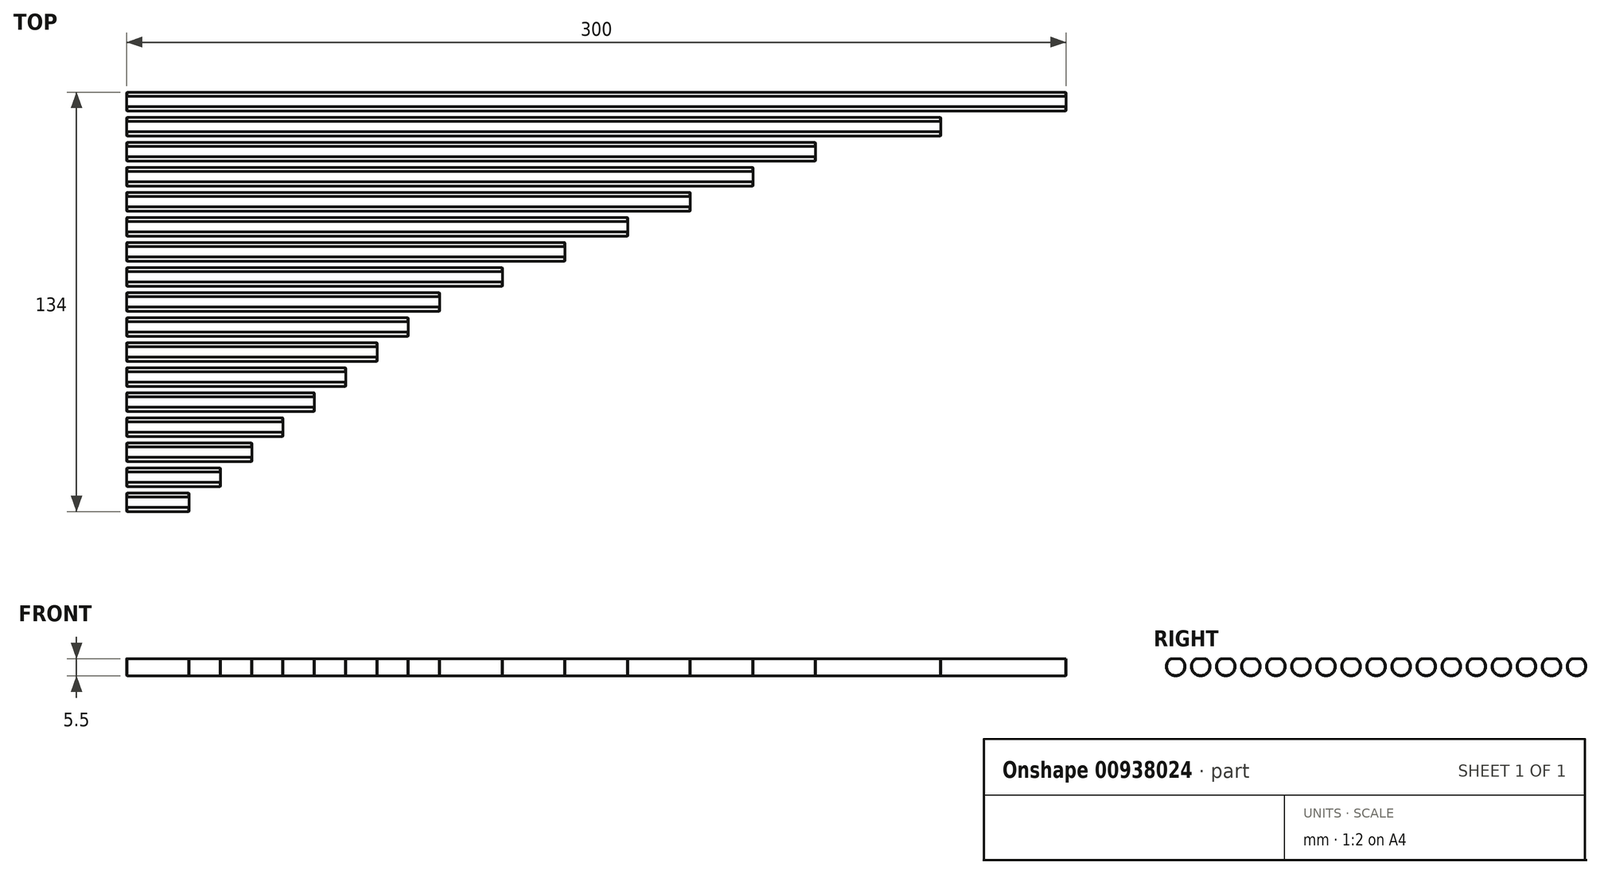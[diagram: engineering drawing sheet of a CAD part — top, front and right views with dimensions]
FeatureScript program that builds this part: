
annotation { "Feature Type Name" : "Feature", "Feature Type Description" : "" }
export const myFeature = defineFeature(function(context is Context, id is Id, definition is map)
    precondition{}
    {
        {
            var Q0;
            Q0=qCreatedBy(makeId("Right.planeOp"),FACE);
            var sketch = newSketch(context, id + "F0", { "sketchPlane" : qUnion([Q0]) });
            skLineSegment(sketch, "E0", {"start": v(0, 3) * mm, "end": v(128, 3) * mm, "construction": true});
            skCircle(sketch, "E1", {"center": v(0, 0) * mm, "radius": 3 * mm});
            skCircle(sketch, "E2", {"center": v(8, 0) * mm, "radius": 3 * mm});
            skCircle(sketch, "E3", {"center": v(16, 0) * mm, "radius": 3 * mm});
            skCircle(sketch, "E4", {"center": v(24, 0) * mm, "radius": 3 * mm});
            skCircle(sketch, "E5", {"center": v(32, 0) * mm, "radius": 3 * mm});
            skCircle(sketch, "E6", {"center": v(40, 0) * mm, "radius": 3 * mm});
            skCircle(sketch, "E7", {"center": v(48, 0) * mm, "radius": 3 * mm});
            skCircle(sketch, "E8", {"center": v(56, 0) * mm, "radius": 3 * mm});
            skCircle(sketch, "E9", {"center": v(64, 0) * mm, "radius": 3 * mm});
            skCircle(sketch, "E10", {"center": v(72, 0) * mm, "radius": 3 * mm});
            skCircle(sketch, "E11", {"center": v(80, 0) * mm, "radius": 3 * mm});
            skLineSegment(sketch, "E12", {"start": v(0, 0) * mm, "end": v(8, 0) * mm, "construction": true});
            skLineSegment(sketch, "E13", {"start": v(16, 0) * mm, "end": v(24, 0) * mm, "construction": true});
            skLineSegment(sketch, "E14", {"start": v(32, 0) * mm, "end": v(40, 0) * mm, "construction": true});
            skLineSegment(sketch, "E15", {"start": v(48, 0) * mm, "end": v(40, 0) * mm, "construction": true});
            skLineSegment(sketch, "E16", {"start": v(24, 0) * mm, "end": v(32, 0) * mm, "construction": true});
            skLineSegment(sketch, "E17", {"start": v(8, 0) * mm, "end": v(16, 0) * mm, "construction": true});
            skLineSegment(sketch, "E18", {"start": v(48, 0) * mm, "end": v(56, 0) * mm, "construction": true});
            skLineSegment(sketch, "E19", {"start": v(56, 0) * mm, "end": v(64, 0) * mm, "construction": true});
            skLineSegment(sketch, "E20", {"start": v(64, 0) * mm, "end": v(72, 0) * mm, "construction": true});
            skLineSegment(sketch, "E21", {"start": v(72, 0) * mm, "end": v(80, 0) * mm, "construction": true});
            skLineSegment(sketch, "E22", {"start": v(80, 0) * mm, "end": v(88, 0) * mm, "construction": true});
            skLineSegment(sketch, "E23", {"start": v(88, 0) * mm, "end": v(96, 0) * mm, "construction": true});
            skLineSegment(sketch, "E24", {"start": v(96, 0) * mm, "end": v(104, 0) * mm, "construction": true});
            skLineSegment(sketch, "E25", {"start": v(104, 0) * mm, "end": v(112, 0) * mm, "construction": true});
            skLineSegment(sketch, "E26", {"start": v(112, 0) * mm, "end": v(120, 0) * mm, "construction": true});
            skCircle(sketch, "E27", {"center": v(88, 0) * mm, "radius": 3 * mm});
            skCircle(sketch, "E28", {"center": v(96, 0) * mm, "radius": 3 * mm});
            skCircle(sketch, "E29", {"center": v(104, 0) * mm, "radius": 3 * mm});
            skCircle(sketch, "E30", {"center": v(112, 0) * mm, "radius": 3 * mm});
            skCircle(sketch, "E31", {"center": v(120, 0) * mm, "radius": 3 * mm});
            skLineSegment(sketch, "E32", {"start": v(120, 0) * mm, "end": v(128, 0) * mm, "construction": true});
            skCircle(sketch, "E33", {"center": v(128, 0) * mm, "radius": 3 * mm});
            skLineSegment(sketch, "E34", {"start": v(-1.66, 2.5) * mm, "end": v(1.66, 2.5) * mm});
            skLineSegment(sketch, "E35.trimOffspring", {"start": v(6.34, 2.5) * mm, "end": v(9.66, 2.5) * mm});
            skLineSegment(sketch, "E36.trimOffspring", {"start": v(14.34, 2.5) * mm, "end": v(17.66, 2.5) * mm});
            skLineSegment(sketch, "E37.trimOffspring", {"start": v(22.34, 2.5) * mm, "end": v(25.66, 2.5) * mm});
            skLineSegment(sketch, "E38.trimOffspring", {"start": v(30.34, 2.5) * mm, "end": v(33.66, 2.5) * mm});
            skLineSegment(sketch, "E39.trimOffspring", {"start": v(38.34, 2.5) * mm, "end": v(41.66, 2.5) * mm});
            skLineSegment(sketch, "E40.trimOffspring", {"start": v(46.34, 2.5) * mm, "end": v(49.66, 2.5) * mm});
            skLineSegment(sketch, "E41.trimOffspring", {"start": v(54.34, 2.5) * mm, "end": v(57.66, 2.5) * mm});
            skLineSegment(sketch, "E42.trimOffspring", {"start": v(62.34, 2.5) * mm, "end": v(65.66, 2.5) * mm});
            skLineSegment(sketch, "E43.trimOffspring", {"start": v(78.34, 2.5) * mm, "end": v(81.66, 2.5) * mm});
            skLineSegment(sketch, "E44.trimOffspring", {"start": v(70.34, 2.5) * mm, "end": v(73.66, 2.5) * mm});
            skLineSegment(sketch, "E45.trimOffspring", {"start": v(86.34, 2.5) * mm, "end": v(89.66, 2.5) * mm});
            skLineSegment(sketch, "E46.trimOffspring", {"start": v(94.34, 2.5) * mm, "end": v(97.66, 2.5) * mm});
            skLineSegment(sketch, "E47.trimOffspring", {"start": v(102.34, 2.5) * mm, "end": v(105.66, 2.5) * mm});
            skLineSegment(sketch, "E48.trimOffspring", {"start": v(110.34, 2.5) * mm, "end": v(113.66, 2.5) * mm});
            skLineSegment(sketch, "E49.trimOffspring", {"start": v(118.34, 2.5) * mm, "end": v(121.66, 2.5) * mm});
            skLineSegment(sketch, "E50.trimOffspring", {"start": v(126.34, 2.5) * mm, "end": v(129.66, 2.5) * mm});
            skSolve(sketch);
        }
        {
            var Q0;
            {var subQ0=sQuery(id+"F0.wireOp",EDGE,"E34");Q0=makeQuery(id+"F0.imprint","IMPRINT",FACE,{"disambiguationData":[TD([[makeQuery(id+"F0.imprint","IMPRINT",EDGE,{"derivedFrom":subQ0}),-1.0]])]});}
            extrude(context, id + "F1", {"entities" : qUnion([Q0]), "depth" : 20 * mm, "offsetDistance" : 25 * mm});
        }
        {
            var Q0;
            {var subQ0=sQuery(id+"F0.wireOp",EDGE,"E35.trimOffspring");Q0=makeQuery(id+"F0.imprint","IMPRINT",FACE,{"disambiguationData":[TD([[makeQuery(id+"F0.imprint","IMPRINT",EDGE,{"derivedFrom":subQ0}),-1.0]])]});}
            extrude(context, id + "F2", {"entities" : qUnion([Q0]), "depth" : 30 * mm, "offsetDistance" : 25 * mm});
        }
        {
            var Q0;
            {var subQ0=sQuery(id+"F0.wireOp",EDGE,"E36.trimOffspring");Q0=makeQuery(id+"F0.imprint","IMPRINT",FACE,{"disambiguationData":[TD([[makeQuery(id+"F0.imprint","IMPRINT",EDGE,{"derivedFrom":subQ0}),-1.0]])]});}
            extrude(context, id + "F3", {"entities" : qUnion([Q0]), "depth" : 40 * mm, "offsetDistance" : 25 * mm});
        }
        {
            var Q0;
            {var subQ0=sQuery(id+"F0.wireOp",EDGE,"E37.trimOffspring");Q0=makeQuery(id+"F0.imprint","IMPRINT",FACE,{"disambiguationData":[TD([[makeQuery(id+"F0.imprint","IMPRINT",EDGE,{"derivedFrom":subQ0}),-1.0]])]});}
            extrude(context, id + "F4", {"entities" : qUnion([Q0]), "depth" : 50 * mm, "offsetDistance" : 25 * mm});
        }
        {
            var Q0;
            {var subQ0=sQuery(id+"F0.wireOp",EDGE,"E38.trimOffspring");Q0=makeQuery(id+"F0.imprint","IMPRINT",FACE,{"disambiguationData":[TD([[makeQuery(id+"F0.imprint","IMPRINT",EDGE,{"derivedFrom":subQ0}),-1.0]])]});}
            extrude(context, id + "F5", {"entities" : qUnion([Q0]), "depth" : 60 * mm, "offsetDistance" : 25 * mm});
        }
        {
            var Q0;
            {var subQ0=sQuery(id+"F0.wireOp",EDGE,"E39.trimOffspring");Q0=makeQuery(id+"F0.imprint","IMPRINT",FACE,{"disambiguationData":[TD([[makeQuery(id+"F0.imprint","IMPRINT",EDGE,{"derivedFrom":subQ0}),-1.0]])]});}
            extrude(context, id + "F6", {"entities" : qUnion([Q0]), "depth" : 70 * mm, "offsetDistance" : 25 * mm});
        }
        {
            var Q0;
            {var subQ0=sQuery(id+"F0.wireOp",EDGE,"E40.trimOffspring");Q0=makeQuery(id+"F0.imprint","IMPRINT",FACE,{"disambiguationData":[TD([[makeQuery(id+"F0.imprint","IMPRINT",EDGE,{"derivedFrom":subQ0}),-1.0]])]});}
            extrude(context, id + "F7", {"entities" : qUnion([Q0]), "depth" : 80 * mm, "offsetDistance" : 25 * mm});
        }
        {
            var Q0;
            {var subQ0=sQuery(id+"F0.wireOp",EDGE,"E41.trimOffspring");Q0=makeQuery(id+"F0.imprint","IMPRINT",FACE,{"disambiguationData":[TD([[makeQuery(id+"F0.imprint","IMPRINT",EDGE,{"derivedFrom":subQ0}),-1.0]])]});}
            extrude(context, id + "F8", {"entities" : qUnion([Q0]), "depth" : 90 * mm, "offsetDistance" : 25 * mm});
        }
        {
            var Q0;
            {var subQ0=sQuery(id+"F0.wireOp",EDGE,"E42.trimOffspring");Q0=makeQuery(id+"F0.imprint","IMPRINT",FACE,{"disambiguationData":[TD([[makeQuery(id+"F0.imprint","IMPRINT",EDGE,{"derivedFrom":subQ0}),-1.0]])]});}
            extrude(context, id + "F9", {"entities" : qUnion([Q0]), "depth" : 100 * mm, "offsetDistance" : 25 * mm});
        }
        {
            var Q0;
            {var subQ0=sQuery(id+"F0.wireOp",EDGE,"E44.trimOffspring");Q0=makeQuery(id+"F0.imprint","IMPRINT",FACE,{"disambiguationData":[TD([[makeQuery(id+"F0.imprint","IMPRINT",EDGE,{"derivedFrom":subQ0}),-1.0]])]});}
            extrude(context, id + "F10", {"entities" : qUnion([Q0]), "depth" : 120 * mm, "offsetDistance" : 25 * mm});
        }
        {
            var Q0;
            {var subQ0=sQuery(id+"F0.wireOp",EDGE,"E43.trimOffspring");Q0=makeQuery(id+"F0.imprint","IMPRINT",FACE,{"disambiguationData":[TD([[makeQuery(id+"F0.imprint","IMPRINT",EDGE,{"derivedFrom":subQ0}),-1.0]])]});}
            extrude(context, id + "F11", {"entities" : qUnion([Q0]), "depth" : 140 * mm, "offsetDistance" : 25 * mm});
        }
        {
            var Q0;
            {var subQ0=sQuery(id+"F0.wireOp",EDGE,"E45.trimOffspring");Q0=makeQuery(id+"F0.imprint","IMPRINT",FACE,{"disambiguationData":[TD([[makeQuery(id+"F0.imprint","IMPRINT",EDGE,{"derivedFrom":subQ0}),-1.0]])]});}
            extrude(context, id + "F12", {"entities" : qUnion([Q0]), "depth" : 160 * mm, "offsetDistance" : 25 * mm});
        }
        {
            var Q0;
            {var subQ0=sQuery(id+"F0.wireOp",EDGE,"E46.trimOffspring");Q0=makeQuery(id+"F0.imprint","IMPRINT",FACE,{"disambiguationData":[TD([[makeQuery(id+"F0.imprint","IMPRINT",EDGE,{"derivedFrom":subQ0}),-1.0]])]});}
            extrude(context, id + "F13", {"entities" : qUnion([Q0]), "depth" : 180 * mm, "offsetDistance" : 25 * mm});
        }
        {
            var Q0;
            {var subQ0=sQuery(id+"F0.wireOp",EDGE,"E47.trimOffspring");Q0=makeQuery(id+"F0.imprint","IMPRINT",FACE,{"disambiguationData":[TD([[makeQuery(id+"F0.imprint","IMPRINT",EDGE,{"derivedFrom":subQ0}),-1.0]])]});}
            extrude(context, id + "F14", {"entities" : qUnion([Q0]), "depth" : 200 * mm, "offsetDistance" : 25 * mm});
        }
        {
            var Q0;
            {var subQ0=sQuery(id+"F0.wireOp",EDGE,"E48.trimOffspring");Q0=makeQuery(id+"F0.imprint","IMPRINT",FACE,{"disambiguationData":[TD([[makeQuery(id+"F0.imprint","IMPRINT",EDGE,{"derivedFrom":subQ0}),-1.0]])]});}
            extrude(context, id + "F15", {"entities" : qUnion([Q0]), "depth" : 220 * mm, "offsetDistance" : 25 * mm});
        }
        {
            var Q0;
            {var subQ0=sQuery(id+"F0.wireOp",EDGE,"E49.trimOffspring");Q0=makeQuery(id+"F0.imprint","IMPRINT",FACE,{"disambiguationData":[TD([[makeQuery(id+"F0.imprint","IMPRINT",EDGE,{"derivedFrom":subQ0}),-1.0]])]});}
            extrude(context, id + "F16", {"entities" : qUnion([Q0]), "depth" : 260 * mm, "offsetDistance" : 25 * mm});
        }
        {
            var Q0;
            {var subQ0=sQuery(id+"F0.wireOp",EDGE,"E50.trimOffspring");Q0=makeQuery(id+"F0.imprint","IMPRINT",FACE,{"disambiguationData":[TD([[makeQuery(id+"F0.imprint","IMPRINT",EDGE,{"derivedFrom":subQ0}),-1.0]])]});}
            extrude(context, id + "F17", {"entities" : qUnion([Q0]), "depth" : 300 * mm, "offsetDistance" : 25 * mm});
        }
        {
            var Q0;
            Q0=makeQuery(id+"F17.opExtrude","CAP_EDGE",EDGE,{"disambiguationData":[OSD([sQuery(id+"F0.wireOp",EDGE,"E33")])],"isStart":true});
            var Q1;
            Q1=makeQuery(id+"F16.opExtrude","CAP_EDGE",EDGE,{"disambiguationData":[OSD([sQuery(id+"F0.wireOp",EDGE,"E31")])],"isStart":true});
            var Q2;
            Q2=makeQuery(id+"F15.opExtrude","CAP_EDGE",EDGE,{"disambiguationData":[OSD([sQuery(id+"F0.wireOp",EDGE,"E30")])],"isStart":true});
            var Q3;
            Q3=makeQuery(id+"F14.opExtrude","CAP_EDGE",EDGE,{"disambiguationData":[OSD([sQuery(id+"F0.wireOp",EDGE,"E29")])],"isStart":true});
            var Q4;
            Q4=makeQuery(id+"F13.opExtrude","CAP_EDGE",EDGE,{"disambiguationData":[OSD([sQuery(id+"F0.wireOp",EDGE,"E28")])],"isStart":true});
            var Q5;
            Q5=makeQuery(id+"F12.opExtrude","CAP_EDGE",EDGE,{"disambiguationData":[OSD([sQuery(id+"F0.wireOp",EDGE,"E27")])],"isStart":true});
            var Q6;
            Q6=makeQuery(id+"F11.opExtrude","CAP_EDGE",EDGE,{"disambiguationData":[OSD([sQuery(id+"F0.wireOp",EDGE,"E11")])],"isStart":true});
            var Q7;
            Q7=makeQuery(id+"F10.opExtrude","CAP_EDGE",EDGE,{"disambiguationData":[OSD([sQuery(id+"F0.wireOp",EDGE,"E10")])],"isStart":true});
            var Q8;
            Q8=makeQuery(id+"F9.opExtrude","CAP_EDGE",EDGE,{"disambiguationData":[OSD([sQuery(id+"F0.wireOp",EDGE,"E9")])],"isStart":true});
            var Q9;
            Q9=makeQuery(id+"F8.opExtrude","CAP_EDGE",EDGE,{"disambiguationData":[OSD([sQuery(id+"F0.wireOp",EDGE,"E8")])],"isStart":true});
            var Q10;
            Q10=makeQuery(id+"F7.opExtrude","CAP_EDGE",EDGE,{"disambiguationData":[OSD([sQuery(id+"F0.wireOp",EDGE,"E7")])],"isStart":true});
            var Q11;
            Q11=makeQuery(id+"F6.opExtrude","CAP_EDGE",EDGE,{"disambiguationData":[OSD([sQuery(id+"F0.wireOp",EDGE,"E6")])],"isStart":true});
            var Q12;
            Q12=makeQuery(id+"F5.opExtrude","CAP_EDGE",EDGE,{"disambiguationData":[OSD([sQuery(id+"F0.wireOp",EDGE,"E5")])],"isStart":true});
            var Q13;
            Q13=makeQuery(id+"F4.opExtrude","CAP_EDGE",EDGE,{"disambiguationData":[OSD([sQuery(id+"F0.wireOp",EDGE,"E4")])],"isStart":true});
            var Q14;
            Q14=makeQuery(id+"F3.opExtrude","CAP_EDGE",EDGE,{"disambiguationData":[OSD([sQuery(id+"F0.wireOp",EDGE,"E3")])],"isStart":true});
            var Q15;
            Q15=makeQuery(id+"F2.opExtrude","CAP_EDGE",EDGE,{"disambiguationData":[OSD([sQuery(id+"F0.wireOp",EDGE,"E2")])],"isStart":true});
            var Q16;
            Q16=makeQuery(id+"F1.opExtrude","CAP_EDGE",EDGE,{"disambiguationData":[OSD([sQuery(id+"F0.wireOp",EDGE,"E1")])],"isStart":true});
            var Q17;
            Q17=makeQuery(id+"F1.opExtrude","CAP_EDGE",EDGE,{"disambiguationData":[OSD([sQuery(id+"F0.wireOp",EDGE,"E1")])],"isStart":false});
            var Q18;
            Q18=makeQuery(id+"F2.opExtrude","CAP_EDGE",EDGE,{"disambiguationData":[OSD([sQuery(id+"F0.wireOp",EDGE,"E2")])],"isStart":false});
            var Q19;
            Q19=makeQuery(id+"F3.opExtrude","CAP_EDGE",EDGE,{"disambiguationData":[OSD([sQuery(id+"F0.wireOp",EDGE,"E3")])],"isStart":false});
            var Q20;
            Q20=makeQuery(id+"F4.opExtrude","CAP_EDGE",EDGE,{"disambiguationData":[OSD([sQuery(id+"F0.wireOp",EDGE,"E4")])],"isStart":false});
            var Q21;
            Q21=makeQuery(id+"F5.opExtrude","CAP_EDGE",EDGE,{"disambiguationData":[OSD([sQuery(id+"F0.wireOp",EDGE,"E5")])],"isStart":false});
            var Q22;
            Q22=makeQuery(id+"F6.opExtrude","CAP_EDGE",EDGE,{"disambiguationData":[OSD([sQuery(id+"F0.wireOp",EDGE,"E6")])],"isStart":false});
            var Q23;
            Q23=makeQuery(id+"F7.opExtrude","CAP_EDGE",EDGE,{"disambiguationData":[OSD([sQuery(id+"F0.wireOp",EDGE,"E7")])],"isStart":false});
            var Q24;
            Q24=makeQuery(id+"F8.opExtrude","CAP_EDGE",EDGE,{"disambiguationData":[OSD([sQuery(id+"F0.wireOp",EDGE,"E8")])],"isStart":false});
            var Q25;
            Q25=makeQuery(id+"F9.opExtrude","CAP_EDGE",EDGE,{"disambiguationData":[OSD([sQuery(id+"F0.wireOp",EDGE,"E9")])],"isStart":false});
            var Q26;
            Q26=makeQuery(id+"F17.opExtrude","CAP_EDGE",EDGE,{"disambiguationData":[OSD([sQuery(id+"F0.wireOp",EDGE,"E33")])],"isStart":false});
            var Q27;
            Q27=makeQuery(id+"F16.opExtrude","CAP_EDGE",EDGE,{"disambiguationData":[OSD([sQuery(id+"F0.wireOp",EDGE,"E31")])],"isStart":false});
            var Q28;
            Q28=makeQuery(id+"F15.opExtrude","CAP_EDGE",EDGE,{"disambiguationData":[OSD([sQuery(id+"F0.wireOp",EDGE,"E30")])],"isStart":false});
            var Q29;
            Q29=makeQuery(id+"F14.opExtrude","CAP_EDGE",EDGE,{"disambiguationData":[OSD([sQuery(id+"F0.wireOp",EDGE,"E29")])],"isStart":false});
            var Q30;
            Q30=makeQuery(id+"F13.opExtrude","CAP_EDGE",EDGE,{"disambiguationData":[OSD([sQuery(id+"F0.wireOp",EDGE,"E28")])],"isStart":false});
            var Q31;
            Q31=makeQuery(id+"F12.opExtrude","CAP_EDGE",EDGE,{"disambiguationData":[OSD([sQuery(id+"F0.wireOp",EDGE,"E27")])],"isStart":false});
            var Q32;
            Q32=makeQuery(id+"F11.opExtrude","CAP_EDGE",EDGE,{"disambiguationData":[OSD([sQuery(id+"F0.wireOp",EDGE,"E11")])],"isStart":false});
            var Q33;
            Q33=makeQuery(id+"F10.opExtrude","CAP_EDGE",EDGE,{"disambiguationData":[OSD([sQuery(id+"F0.wireOp",EDGE,"E10")])],"isStart":false});
            chamfer(context, id + "F18", {"entities" : qUnion([Q0, Q1, Q2, Q3, Q4, Q5, Q6, Q7, Q8, Q9, Q10, Q11, Q12, Q13, Q14, Q15, Q16, Q17, Q18, Q19, Q20, Q21, Q22, Q23, Q24, Q25, Q26, Q27, Q28, Q29, Q30, Q31, Q32, Q33]), "width" : 0.12 * mm, "tangentPropagation" : true});
        }
    });
